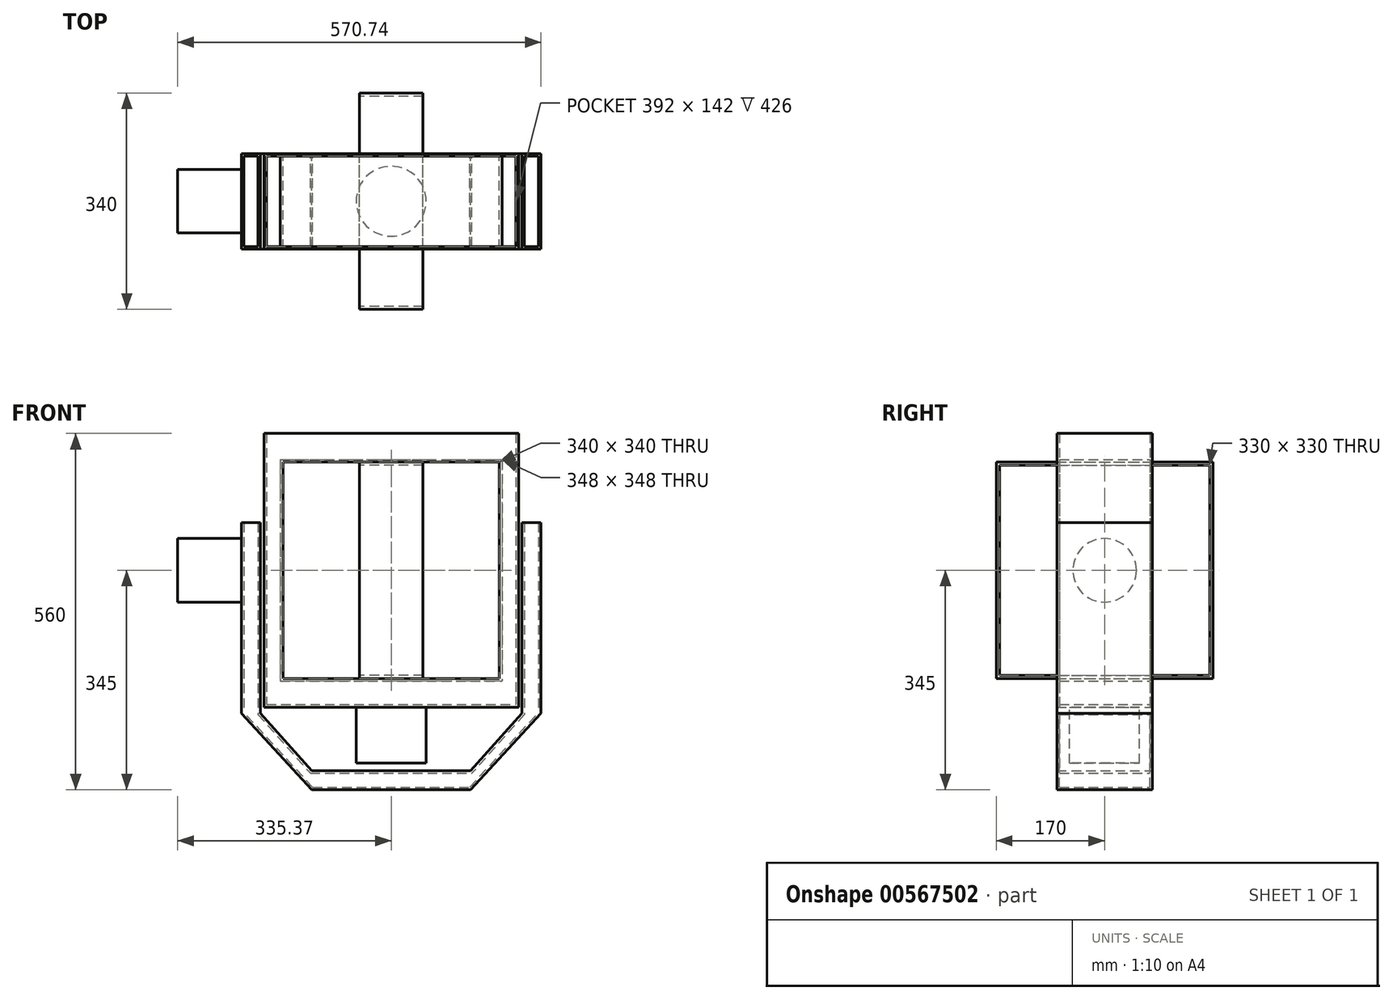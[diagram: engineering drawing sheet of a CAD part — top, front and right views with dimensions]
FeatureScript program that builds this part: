
annotation { "Feature Type Name" : "Feature", "Feature Type Description" : "" }
export const myFeature = defineFeature(function(context is Context, id is Id, definition is map)
    precondition{}
    {
        {
            var Q0;
            Q0=qCreatedBy(makeId("Right.planeOp"),FACE);
            var sketch = newSketch(context, id + "F0", { "sketchPlane" : qUnion([Q0])});
            skLineSegment(sketch, "E0.bottom", {"start": v(-170, 170) * mm, "end": v(170, 170) * mm});
            skLineSegment(sketch, "E0.top", {"start": v(-170, -170) * mm, "end": v(170, -170) * mm});
            skLineSegment(sketch, "E0.left", {"start": v(-170, 170) * mm, "end": v(-170, -170) * mm});
            skLineSegment(sketch, "E0.right", {"start": v(170, 170) * mm, "end": v(170, -170) * mm});
            skLineSegment(sketch, "E1", {"start": v(-170, 0) * mm, "end": v(170, 0) * mm, "construction": true});
            skLineSegment(sketch, "E2.bottom", {"start": v(-165, 165) * mm, "end": v(165, 165) * mm});
            skLineSegment(sketch, "E2.top", {"start": v(-165, -165) * mm, "end": v(165, -165) * mm});
            skLineSegment(sketch, "E2.left", {"start": v(-165, 165) * mm, "end": v(-165, -165) * mm});
            skLineSegment(sketch, "E2.right", {"start": v(165, 165) * mm, "end": v(165, -165) * mm});
            skLineSegment(sketch, "E3", {"start": v(-165, 0) * mm, "end": v(165, 0) * mm, "construction": true});
            skSolve(sketch);
        }
        {
            var Q0;
            Q0 = qSketchRegion(id + "F0", true);
            extrude(context, id + "F1", {"entities" : qUnion([Q0]), "endBound" : BoundingType.SYMMETRIC, "depth" : 100 * mm, "offsetDistance" : 25 * mm});
        }
        {
            var Q0;
            Q0=qCreatedBy(makeId("Front.planeOp"),FACE);
            var sketch = newSketch(context, id + "F2", { "sketchPlane" : qUnion([Q0])});
            skLineSegment(sketch, "E4.bottom", {"start": v(-170, 170) * mm, "end": v(170, 170) * mm});
            skLineSegment(sketch, "E4.top", {"start": v(-170, -170) * mm, "end": v(170, -170) * mm});
            skLineSegment(sketch, "E4.left", {"start": v(-170, 170) * mm, "end": v(-170, -170) * mm});
            skLineSegment(sketch, "E4.right", {"start": v(170, 170) * mm, "end": v(170, -170) * mm});
            skLineSegment(sketch, "E5", {"start": v(-170, 0) * mm, "end": v(170, 0) * mm, "construction": true});
            skLineSegment(sketch, "E6.bottom", {"start": v(-200, 215) * mm, "end": v(200, 215) * mm});
            skLineSegment(sketch, "E6.top", {"start": v(-200, -215) * mm, "end": v(200, -215) * mm});
            skLineSegment(sketch, "E6.left", {"start": v(-200, 215) * mm, "end": v(-200, -215) * mm});
            skLineSegment(sketch, "E6.right", {"start": v(200, 215) * mm, "end": v(200, -215) * mm});
            skPoint(sketch, "E6.middle", {"position": v(0, 0) * mm});
            skSolve(sketch);
        }
        {
            var Q0;
            Q0 = qSketchRegion(id + "F2", true);
            extrude(context, id + "F3", {"entities" : qUnion([Q0]), "endBound" : BoundingType.SYMMETRIC, "depth" : 150 * mm, "offsetDistance" : 25 * mm});
        }
        {
            var Q0;
            Q0=qCreatedBy(makeId("Front.planeOp"),FACE);
            var sketch = newSketch(context, id + "F4", { "sketchPlane" : qUnion([Q0])});
            skLineSegment(sketch, "E7.bottom", {"start": v(-235.37, 75) * mm, "end": v(-205.37, 75) * mm});
            skLineSegment(sketch, "E7.top", {"start": v(-235.37, -225) * mm, "end": v(-205.37, -225) * mm});
            skLineSegment(sketch, "E7.left", {"start": v(-235.37, 75) * mm, "end": v(-235.37, -225) * mm});
            skLineSegment(sketch, "E7.right", {"start": v(-205.37, 75) * mm, "end": v(-205.37, -225) * mm});
            skLineSegment(sketch, "E8.bottom", {"start": v(-125, -315) * mm, "end": v(125, -315) * mm});
            skLineSegment(sketch, "E8.top", {"start": v(-125, -345) * mm, "end": v(125, -345) * mm});
            skLineSegment(sketch, "E8.left", {"start": v(-125, -315) * mm, "end": v(-125, -345) * mm});
            skLineSegment(sketch, "E8.right", {"start": v(125, -315) * mm, "end": v(125, -345) * mm});
            skLineSegment(sketch, "E9", {"start": v(0, 0) * mm, "end": v(0, -315) * mm, "construction": true});
            skLineSegment(sketch, "E10", {"start": v(-205.37, -225) * mm, "end": v(-125, -315) * mm});
            skLineSegment(sketch, "E11", {"start": v(-125, -345) * mm, "end": v(-235.37, -225) * mm});
            skLineSegment(sketch, "E12.MirrorCS", {"start": v(235.37, 75) * mm, "end": v(235.37, -225) * mm});
            skLineSegment(sketch, "E13.MirrorCS", {"start": v(205.37, 75) * mm, "end": v(205.37, -225) * mm});
            skLineSegment(sketch, "E14.MirrorCS", {"start": v(235.37, 75) * mm, "end": v(205.37, 75) * mm});
            skLineSegment(sketch, "E15.MirrorCS", {"start": v(205.37, -225) * mm, "end": v(125, -315) * mm});
            skLineSegment(sketch, "E16.MirrorCS", {"start": v(125, -345) * mm, "end": v(235.37, -225) * mm});
            skSolve(sketch);
        }
        {
            var Q0;
            Q0 = qSketchRegion(id + "F4", true);
            extrude(context, id + "F5", {"entities" : qUnion([Q0]), "endBound" : BoundingType.SYMMETRIC, "depth" : 150 * mm, "offsetDistance" : 25 * mm});
        }
        {
            var Q0;
            Q0=makeQuery(id+"F5.opExtrude","SWEPT_FACE",FACE,{"disambiguationData":[OSD([sQuery(id+"F4.wireOp",EDGE,"E7.bottom")])]});
            var Q1;
            Q1=makeQuery(id+"F5.opExtrude","SWEPT_FACE",FACE,{"disambiguationData":[OSD([sQuery(id+"F4.wireOp",EDGE,"E14.MirrorCS")])]});
            shell(context, id + "F6", {"entities" : qUnion([Q0, Q1]), "thickness" : 4 * mm});
        }
        {
            var Q0;
            Q0=makeQuery(id+"F5.opExtrude","SWEPT_FACE",FACE,{"disambiguationData":[OSD([sQuery(id+"F4.wireOp",EDGE,"E7.left")])]});
            var sketch = newSketch(context, id + "F7", { "sketchPlane" : qUnion([Q0])});
            skCircle(sketch, "E17", {"center": v(0, 0) * mm, "radius": 50 * mm});
            skSolve(sketch);
        }
        {
            var Q0;
            Q0=makeQuery(id+"F3.opExtrude","SWEPT_FACE",FACE,{"disambiguationData":[OSD([sQuery(id+"F2.wireOp",EDGE,"E6.bottom")])]});
            shell(context, id + "F8", {"entities" : qUnion([Q0]), "thickness" : 4 * mm});
        }
        {
            var Q0;
            Q0 = qSketchRegion(id + "F7", true);
            extrude(context, id + "F9", {"entities" : qUnion([Q0]), "operationType" : NewBodyOperationType.ADD, "depth" : 100 * mm, "offsetDistance" : 25 * mm});
        }
        {
            var Q0;
            Q0=makeQuery(id+"F3.opExtrude","SWEPT_FACE",FACE,{"disambiguationData":[OSD([sQuery(id+"F2.wireOp",EDGE,"E6.top")])]});
            var sketch = newSketch(context, id + "F10", { "sketchPlane" : qUnion([Q0])});
            skCircle(sketch, "E18", {"center": v(0, 0) * mm, "radius": 55 * mm});
            skLineSegment(sketch, "E19", {"start": v(-200, 0) * mm, "end": v(200, 0) * mm, "construction": true});
            skSolve(sketch);
        }
        {
            var Q0;
            Q0 = qSketchRegion(id + "F10", true);
            extrude(context, id + "F11", {"entities" : qUnion([Q0]), "operationType" : NewBodyOperationType.ADD, "depth" : 88 * mm, "offsetDistance" : 25 * mm});
        }
    });
